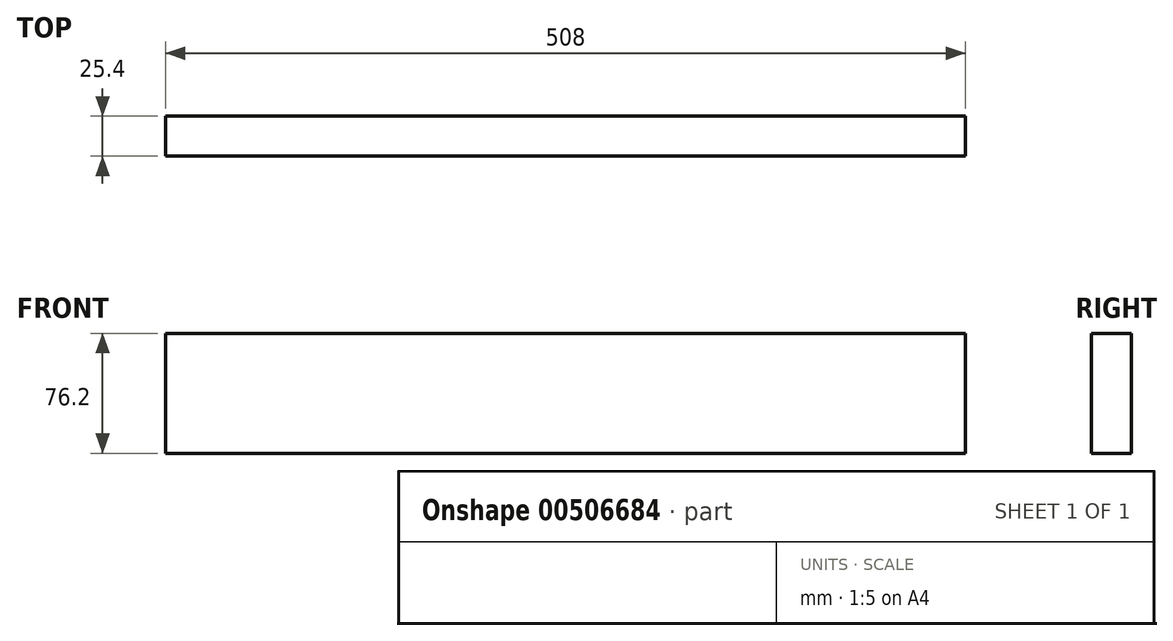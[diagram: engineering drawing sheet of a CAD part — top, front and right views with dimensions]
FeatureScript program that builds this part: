
annotation { "Feature Type Name" : "Feature", "Feature Type Description" : "" }
export const myFeature = defineFeature(function(context is Context, id is Id, definition is map)
    precondition{}
    {
        {
            var Q0;
            Q0=qCreatedBy(makeId("Right.planeOp"),FACE);
            var sketch = newSketch(context, id + "F0", { "sketchPlane" : qUnion([Q0])});
            skLineSegment(sketch, "E0.bottom", {"start": v(12.7, 38.1) * mm, "end": v(-12.7, 38.1) * mm});
            skLineSegment(sketch, "E0.top", {"start": v(12.7, -38.1) * mm, "end": v(-12.7, -38.1) * mm});
            skLineSegment(sketch, "E0.left", {"start": v(12.7, 38.1) * mm, "end": v(12.7, -38.1) * mm});
            skLineSegment(sketch, "E0.right", {"start": v(-12.7, 38.1) * mm, "end": v(-12.7, -38.1) * mm});
            skPoint(sketch, "E0.middle", {"position": v(0, 0) * mm});
            skSolve(sketch);
        }
        {
            var Q0;
            Q0=makeQuery(id+"F0.imprint","IMPRINT",FACE,{"disambiguationData":[TD([[makeQuery(id+"F0.imprint","IMPRINT",EDGE,{"derivedFrom":sQuery(id+"F0.wireOp",EDGE,"E0.bottom")}),1.0]])]});
            extrude(context, id + "F1", {"entities" : qUnion([Q0]), "endBound" : BoundingType.SYMMETRIC, "depth" : 508 * mm});
        }
    });
